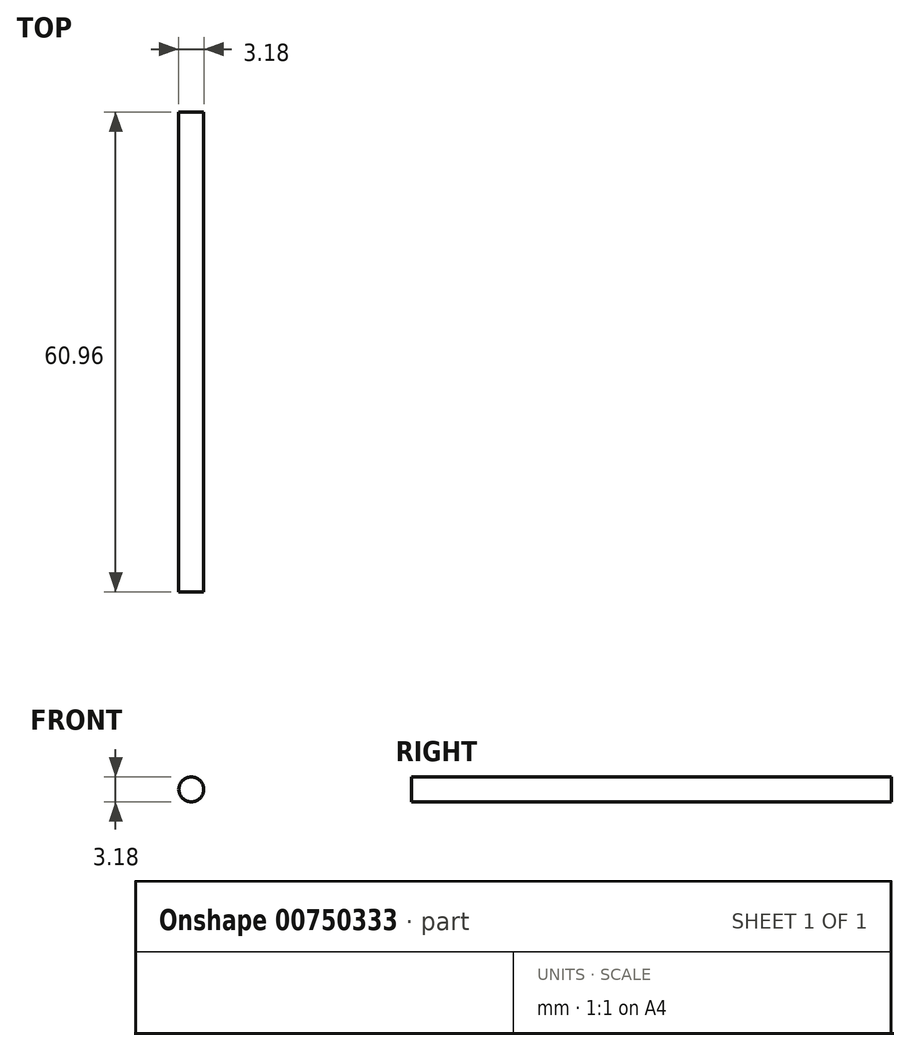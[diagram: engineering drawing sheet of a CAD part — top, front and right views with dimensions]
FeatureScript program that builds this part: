
annotation { "Feature Type Name" : "Feature", "Feature Type Description" : "" }
export const myFeature = defineFeature(function(context is Context, id is Id, definition is map)
    precondition{}
    {
        {
            var Q0;
            Q0=qCreatedBy(makeId("Front.planeOp"),FACE);
            var sketch = newSketch(context, id + "F0", { "sketchPlane" : qUnion([Q0])});
            skCircle(sketch, "E0", {"center": v(0, 0) * mm, "radius": 1.59 * mm});
            skSolve(sketch);
        }
        {
            var Q0;
            Q0 = qSketchRegion(id + "F0", true);
            extrude(context, id + "F1", {"entities" : qUnion([Q0]), "depth" : 60.96 * mm, "offsetDistance" : 25.4 * mm});
        }
    });
